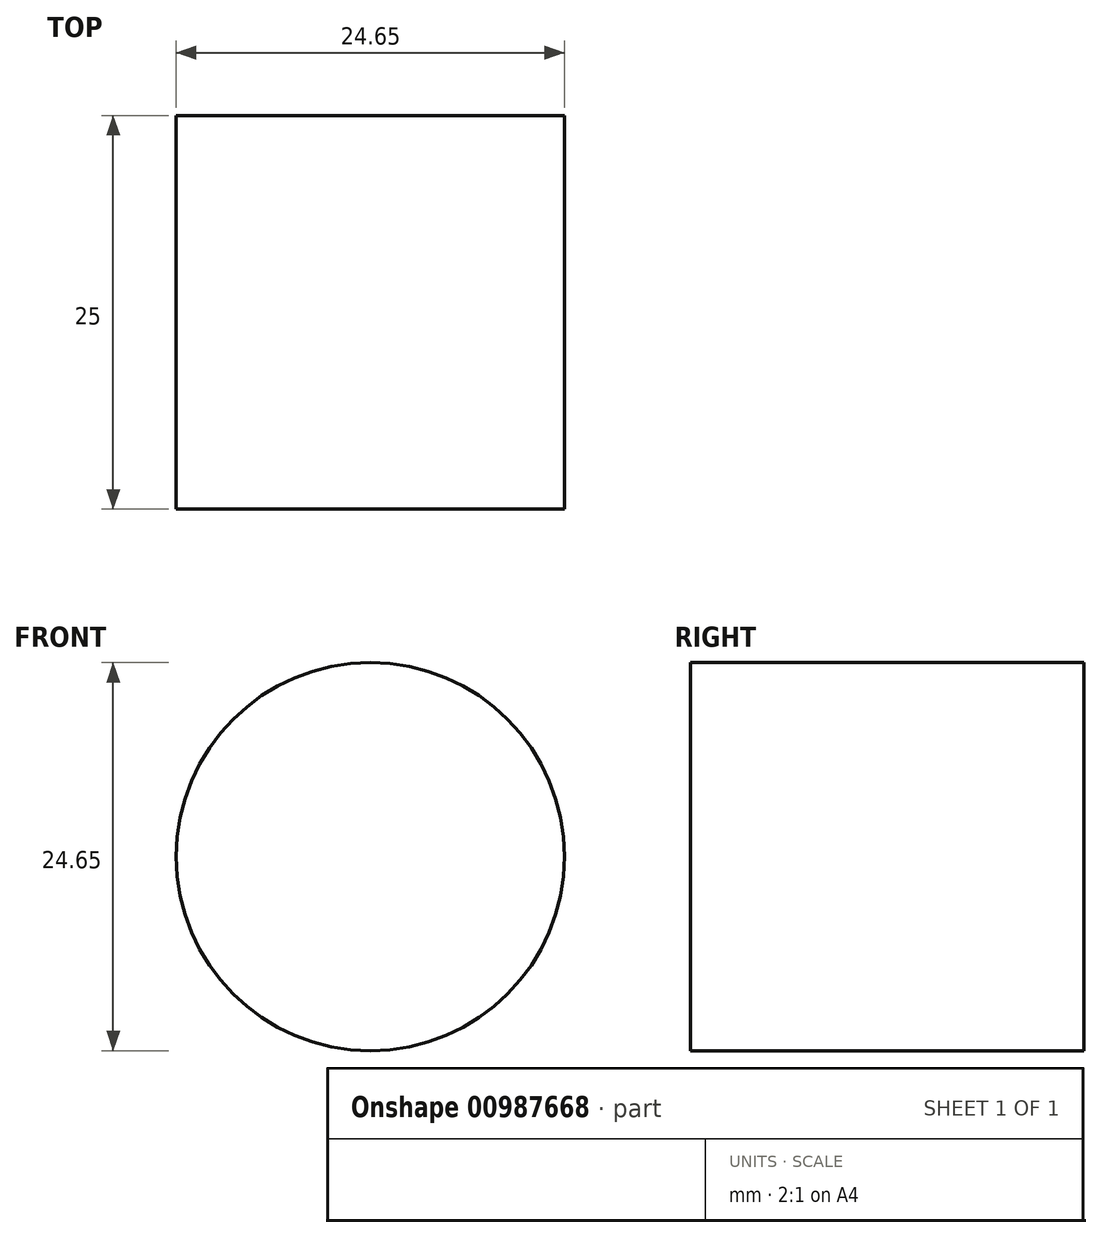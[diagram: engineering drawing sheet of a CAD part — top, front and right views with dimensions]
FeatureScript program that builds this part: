
annotation { "Feature Type Name" : "Feature", "Feature Type Description" : "" }
export const myFeature = defineFeature(function(context is Context, id is Id, definition is map)
    precondition{}
    {
        {
            var Q0;
            Q0=qCreatedBy(makeId("Front.planeOp"),FACE);
            var sketch = newSketch(context, id + "F0", { "sketchPlane" : qUnion([Q0])});
            skCircle(sketch, "E0", {"center": v(-22.06, 14.2) * mm, "radius": 12.33 * mm});
            skSolve(sketch);
        }
        {
            var Q0;
            Q0 = qSketchRegion(id + "F0", true);
            extrude(context, id + "F1", {"entities" : qUnion([Q0]), "depth" : 25 * mm, "offsetDistance" : 25 * mm});
        }
    });
